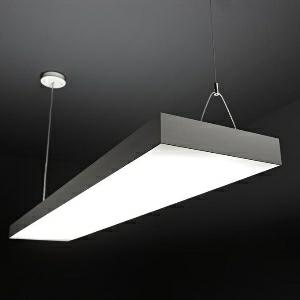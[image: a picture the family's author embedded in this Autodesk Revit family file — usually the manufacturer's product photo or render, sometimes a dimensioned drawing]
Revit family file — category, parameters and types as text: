
# Revit family: spectral_norea_norea-p_1050_9180_840_mps_0d9e
name_source: partatom
category: Lighting Fixtures
revit_build: Autodesk Revit 2016 (Build: 20150220_1215(x64)
units: mm (PartAtom-declared; Revit-internal decimal feet)

## family parameters
Cut with Voids When Loaded = No
Host = Face
Light Source = No
Part Type = Normal
Room Calculation Point = No
Round Connector Dimension = Use Diameter
Shared = No

## types (1)
- SPECTRAL NOREA (1 x )
    Apparent Load = 0 VA
    Approval mark = CE
    CIE Flux Codes = 72 93 98 75 75
    Control Gear = Electronic transformer
    Default Elevation = 1800 mm
    Description = SPT0000093
NOREA Pendant luminaire

Design:
Square luminaire element with a microprism panel in a natural anodised aluminium profile frame surround. The luminaire is suspended by a wire pendant with ceiling holder and transparent connecting cable with rectangular powder-coated ceiling junction box. Cable length adjustable at the junction box, steel wire steplessly height adjustable at the luminaire. The electrical gear is accommodated under a cover at the top of the luminaire. This can be removed using key holes for maintenance work. The indirect component for brightening the ceiling is provided by LED linear modules at the top of the luminaire. The LED module is formed as a rectangular LED flat board. Luminaire with heat-resistant wiring. Variant suitable for office use with a microprism panel MPS. The LED points are visible as circles on the microprism panel. Also in a dimmable version.

Colour:
Housing – similar to RAL 9016 White silk matt;
Frame – natural anodised
    Height = 50 mm
    Lamp = 1 x
    Lamp count = 1
    Length = 1050 mm
    Luminous efficacy = 0 lm/W
    Manufacturer = Ridi
    ModVariant = No
    Model = NOREA-P 1050/9180/840 MPS
    Mounting Place = Ceiling
    Mounting Type = Pendant
    Number of Poles = 1
    OnlyDefault = Yes
    Power Factor = 1
    Product Name = SPECTRAL NOREA
    Product group = Pendant luminaire
    ProductGroupID = 9
    Protection Class = Protection class
    Protection Degree = IP 20
    RlxData = <blob elided: 41669 chars, md5=40376828>
    Socket = socket
    Standby Power = 0 W
    System Light Flux = 0 lm
    System Power = 0 W
    Type Image = norea01.jpg
    URL = http://reluxnet.relux.com
    VarID = 1
    Voltage = 0 V
    Weight = 0.00 kg
    Width = 312 mm

## geometry (parser evidence)
native form markers: Sweep x13
no freeform markers — native parametric forms only
